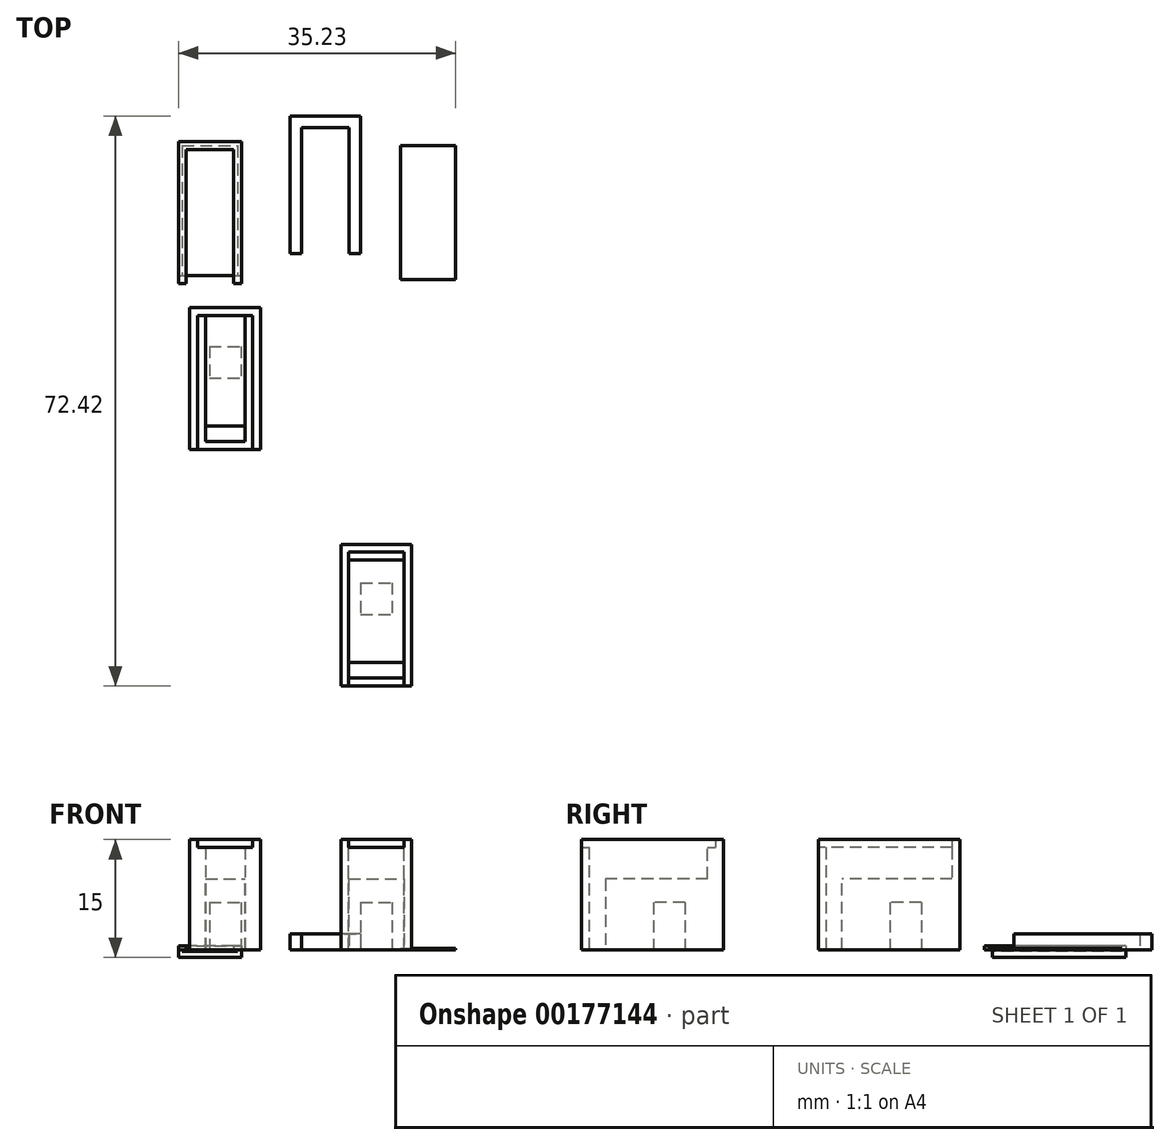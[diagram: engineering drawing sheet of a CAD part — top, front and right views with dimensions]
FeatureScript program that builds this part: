
annotation { "Feature Type Name" : "Feature", "Feature Type Description" : "" }
export const myFeature = defineFeature(function(context is Context, id is Id, definition is map)
    precondition{}
    {
        {
            var Q0;
            Q0=qCreatedBy(makeId("Top.planeOp"),FACE);
            var sketch = newSketch(context, id + "F0", { "sketchPlane" : qUnion([Q0])});
            skLineSegment(sketch, "E0.bottom", {"start": v(4.5, -9) * mm, "end": v(-4.5, -9) * mm});
            skLineSegment(sketch, "E0.top", {"start": v(4.5, 9) * mm, "end": v(-4.5, 9) * mm});
            skLineSegment(sketch, "E0.left", {"start": v(4.5, -9) * mm, "end": v(4.5, 9) * mm});
            skLineSegment(sketch, "E0.right", {"start": v(-4.5, -9) * mm, "end": v(-4.5, 9) * mm});
            skPoint(sketch, "E0.middle", {"position": v(0, 0) * mm});
            skSolve(sketch);
        }
        {
            var Q0;
            Q0 = qSketchRegion(id + "F0", true);
            extrude(context, id + "F1", {"entities" : qUnion([Q0]), "depth" : 13 * mm});
        }
        {
            var Q0;
            Q0=makeQuery(id+"F1.opExtrude","CAP_FACE",FACE,{"disambiguationData":[OSD([sQuery(id+"F0.wireOp",EDGE,"E0.bottom"),sQuery(id+"F0.wireOp",EDGE,"E0.top"),sQuery(id+"F0.wireOp",EDGE,"E0.left"),sQuery(id+"F0.wireOp",EDGE,"E0.right")])],"isStart":true});
            var sketch = newSketch(context, id + "F2", { "sketchPlane" : qUnion([Q0])});
            skLineSegment(sketch, "E1.bottom", {"start": v(-2, -4.1) * mm, "end": v(2, -4.1) * mm});
            skLineSegment(sketch, "E1.top", {"start": v(-2, -0.1) * mm, "end": v(2, -0.1) * mm});
            skLineSegment(sketch, "E1.left", {"start": v(-2, -4.1) * mm, "end": v(-2, -0.1) * mm});
            skLineSegment(sketch, "E1.right", {"start": v(2, -4.1) * mm, "end": v(2, -0.1) * mm});
            skPoint(sketch, "E1.middle", {"position": v(0, -2.1) * mm});
            skSolve(sketch);
        }
        {
            var Q0;
            Q0 = qSketchRegion(id + "F2", true);
            extrude(context, id + "F3", {"entities" : qUnion([Q0]), "operationType" : NewBodyOperationType.REMOVE, "oppositeDirection" : true, "depth" : 6 * mm});
        }
        {
            var Q0;
            Q0=makeQuery(id+"F1.opExtrude","SWEPT_FACE",FACE,{"disambiguationData":[OSD([sQuery(id+"F0.wireOp",EDGE,"E0.bottom")])]});
            var sketch = newSketch(context, id + "F4", { "sketchPlane" : qUnion([Q0])});
            skLineSegment(sketch, "E2.bottom", {"start": v(-2.5, 13) * mm, "end": v(2.5, 13) * mm});
            skLineSegment(sketch, "E2.top", {"start": v(-2.5, 9) * mm, "end": v(2.5, 9) * mm});
            skLineSegment(sketch, "E2.left", {"start": v(-2.5, 13) * mm, "end": v(-2.5, 9) * mm});
            skLineSegment(sketch, "E2.right", {"start": v(2.5, 13) * mm, "end": v(2.5, 9) * mm});
            skSolve(sketch);
        }
        {
            var Q0;
            Q0 = qSketchRegion(id + "F4", true);
            extrude(context, id + "F5", {"entities" : qUnion([Q0]), "operationType" : NewBodyOperationType.REMOVE, "oppositeDirection" : true, "depth" : 17 * mm});
        }
        {
            var Q0;
            Q0=qCreatedBy(makeId("Top.planeOp"),FACE);
            var sketch = newSketch(context, id + "F6", { "sketchPlane" : qUnion([Q0])});
            skLineSegment(sketch, "E3", {"start": v(-5.95, 12.1) * mm, "end": v(-5.95, 30.1) * mm});
            skLineSegment(sketch, "E4", {"start": v(-5.95, 30.1) * mm, "end": v(2.05, 30.1) * mm});
            skLineSegment(sketch, "E5", {"start": v(2.05, 30.1) * mm, "end": v(2.05, 12.1) * mm});
            skLineSegment(sketch, "E6", {"start": v(2.05, 12.1) * mm, "end": v(1.05, 12.1) * mm});
            skLineSegment(sketch, "E7", {"start": v(1.05, 12.1) * mm, "end": v(1.05, 29.1) * mm});
            skLineSegment(sketch, "E8", {"start": v(1.05, 29.1) * mm, "end": v(-4.95, 29.1) * mm});
            skLineSegment(sketch, "E9", {"start": v(-4.95, 29.1) * mm, "end": v(-4.95, 12.1) * mm});
            skLineSegment(sketch, "E10", {"start": v(-4.95, 12.1) * mm, "end": v(-5.95, 12.1) * mm});
            skSolve(sketch);
        }
        {
            var Q0;
            Q0 = qSketchRegion(id + "F6", true);
            extrude(context, id + "F7", {"entities" : qUnion([Q0]), "depth" : 0.5 * mm});
        }
        {
            var Q0;
            Q0=qCreatedBy(makeId("Top.planeOp"),FACE);
            var sketch = newSketch(context, id + "F8", { "sketchPlane" : qUnion([Q0])});
            skLineSegment(sketch, "E11.bottom", {"start": v(-5.95, 13.1) * mm, "end": v(2.05, 13.1) * mm});
            skLineSegment(sketch, "E11.top", {"start": v(-5.95, 30.1) * mm, "end": v(2.05, 30.1) * mm});
            skLineSegment(sketch, "E11.left", {"start": v(-5.95, 13.1) * mm, "end": v(-5.95, 30.1) * mm});
            skLineSegment(sketch, "E11.right", {"start": v(2.05, 13.1) * mm, "end": v(2.05, 30.1) * mm});
            skSolve(sketch);
        }
        {
            var Q0;
            Q0 = qSketchRegion(id + "F8", true);
            extrude(context, id + "F9", {"entities" : qUnion([Q0]), "oppositeDirection" : true, "depth" : 1 * mm});
        }
        {
            var Q0;
            Q0=makeQuery(id+"F9.opExtrude","SWEPT_FACE",FACE,{"disambiguationData":[OSD([sQuery(id+"F8.wireOp",EDGE,"E11.bottom")])]});
            var sketch = newSketch(context, id + "F10", { "sketchPlane" : qUnion([Q0])});
            skLineSegment(sketch, "E12.bottom", {"start": v(-5.45, 0) * mm, "end": v(1.55, 0) * mm});
            skLineSegment(sketch, "E12.top", {"start": v(-5.45, -0.2) * mm, "end": v(1.55, -0.2) * mm});
            skLineSegment(sketch, "E12.left", {"start": v(-5.45, 0) * mm, "end": v(-5.45, -0.2) * mm});
            skLineSegment(sketch, "E12.right", {"start": v(1.55, 0) * mm, "end": v(1.55, -0.2) * mm});
            skSolve(sketch);
        }
        {
            var Q0;
            Q0 = qSketchRegion(id + "F10", true);
            extrude(context, id + "F11", {"entities" : qUnion([Q0]), "operationType" : NewBodyOperationType.REMOVE, "oppositeDirection" : true, "depth" : 16.5 * mm});
        }
        {
            var Q0;
            Q0=qCreatedBy(makeId("Top.planeOp"),FACE);
            var sketch = newSketch(context, id + "F12", { "sketchPlane" : qUnion([Q0])});
            skLineSegment(sketch, "E13", {"start": v(8.22, 15.87) * mm, "end": v(8.22, 33.37) * mm});
            skLineSegment(sketch, "E14", {"start": v(8.22, 33.37) * mm, "end": v(17.22, 33.37) * mm});
            skLineSegment(sketch, "E15", {"start": v(17.22, 33.37) * mm, "end": v(17.22, 15.87) * mm});
            skLineSegment(sketch, "E16", {"start": v(17.22, 15.87) * mm, "end": v(15.72, 15.87) * mm});
            skLineSegment(sketch, "E17", {"start": v(15.72, 15.87) * mm, "end": v(15.72, 31.87) * mm});
            skLineSegment(sketch, "E18", {"start": v(15.72, 31.87) * mm, "end": v(9.72, 31.87) * mm});
            skLineSegment(sketch, "E19", {"start": v(9.72, 31.87) * mm, "end": v(9.72, 15.87) * mm});
            skLineSegment(sketch, "E20", {"start": v(9.72, 15.87) * mm, "end": v(8.22, 15.87) * mm});
            skSolve(sketch);
        }
        {
            var Q0;
            Q0 = qSketchRegion(id + "F12", true);
            extrude(context, id + "F13", {"entities" : qUnion([Q0]), "depth" : 2 * mm});
        }
        {
            var Q0;
            Q0=qCreatedBy(makeId("Top.planeOp"),FACE);
            var sketch = newSketch(context, id + "F14", { "sketchPlane" : qUnion([Q0])});
            skLineSegment(sketch, "E21.bottom", {"start": v(22.28, 12.58) * mm, "end": v(29.28, 12.58) * mm});
            skLineSegment(sketch, "E21.top", {"start": v(22.28, 29.58) * mm, "end": v(29.28, 29.58) * mm});
            skLineSegment(sketch, "E21.left", {"start": v(22.28, 12.58) * mm, "end": v(22.28, 29.58) * mm});
            skLineSegment(sketch, "E21.right", {"start": v(29.28, 12.58) * mm, "end": v(29.28, 29.58) * mm});
            skSolve(sketch);
        }
        {
            var Q0;
            Q0 = qSketchRegion(id + "F14", true);
            extrude(context, id + "F15", {"entities" : qUnion([Q0]), "depth" : 0.2 * mm});
        }
        {
            var Q0;
            Q0=makeQuery(id+"F5.boolean.opBoolean","COPY",FACE,{"derivedFrom":makeQuery(id+"F5.opExtrude","SWEPT_FACE",FACE,{"disambiguationData":[OSD([sQuery(id+"F4.wireOp",EDGE,"E2.top")])]})});
            var sketch = newSketch(context, id + "F16", { "sketchPlane" : qUnion([Q0])});
            skLineSegment(sketch, "E22.bottom", {"start": v(-2.5, -9) * mm, "end": v(2.5, -9) * mm});
            skLineSegment(sketch, "E22.top", {"start": v(-2.5, -6) * mm, "end": v(2.5, -6) * mm});
            skLineSegment(sketch, "E22.left", {"start": v(-2.5, -9) * mm, "end": v(-2.5, -6) * mm});
            skLineSegment(sketch, "E22.right", {"start": v(2.5, -9) * mm, "end": v(2.5, -6) * mm});
            skSolve(sketch);
        }
        {
            var Q0;
            Q0 = qSketchRegion(id + "F16", true);
            extrude(context, id + "F17", {"entities" : qUnion([Q0]), "operationType" : NewBodyOperationType.REMOVE, "oppositeDirection" : true, "depth" : 25 * mm});
        }
        {
            var Q0;
            Q0=makeQuery(id+"F1.opExtrude","CAP_FACE",FACE,{"disambiguationData":[OSD([sQuery(id+"F0.wireOp",EDGE,"E0.bottom"),sQuery(id+"F0.wireOp",EDGE,"E0.top"),sQuery(id+"F0.wireOp",EDGE,"E0.left"),sQuery(id+"F0.wireOp",EDGE,"E0.right")])],"isStart":false});
            var sketch = newSketch(context, id + "F18", { "sketchPlane" : qUnion([Q0])});
            skLineSegment(sketch, "E23", {"start": v(-4.5, -9) * mm, "end": v(-4.5, 9) * mm});
            skLineSegment(sketch, "E24", {"start": v(-4.5, 9) * mm, "end": v(4.5, 9) * mm});
            skLineSegment(sketch, "E25", {"start": v(4.5, 9) * mm, "end": v(4.5, -9) * mm});
            skLineSegment(sketch, "E26", {"start": v(4.5, -9) * mm, "end": v(3.5, -9) * mm});
            skLineSegment(sketch, "E27", {"start": v(3.5, -9) * mm, "end": v(3.5, 8) * mm});
            skLineSegment(sketch, "E28", {"start": v(3.5, 8) * mm, "end": v(-3.5, 8) * mm});
            skLineSegment(sketch, "E29", {"start": v(-3.5, 8) * mm, "end": v(-3.5, -9) * mm});
            skLineSegment(sketch, "E30", {"start": v(-3.5, -9) * mm, "end": v(-4.5, -9) * mm});
            skSolve(sketch);
        }
        {
            var Q0;
            Q0 = qSketchRegion(id + "F18", true);
            extrude(context, id + "F19", {"entities" : qUnion([Q0]), "operationType" : NewBodyOperationType.ADD, "depth" : 1 * mm});
        }
        {
            var Q0;
            Q0=makeQuery(id+"F1.opExtrude","CAP_FACE",FACE,{"disambiguationData":[OSD([sQuery(id+"F0.wireOp",EDGE,"E0.bottom"),sQuery(id+"F0.wireOp",EDGE,"E0.top"),sQuery(id+"F0.wireOp",EDGE,"E0.left"),sQuery(id+"F0.wireOp",EDGE,"E0.right")])],"isStart":true});
            var sketch = newSketch(context, id + "F20", { "sketchPlane" : qUnion([Q0])});
            skLineSegment(sketch, "E31.bottom", {"start": v(2.5, 9) * mm, "end": v(-2.5, 9) * mm});
            skLineSegment(sketch, "E31.top", {"start": v(2.5, 8) * mm, "end": v(-2.5, 8) * mm});
            skLineSegment(sketch, "E31.left", {"start": v(2.5, 9) * mm, "end": v(2.5, 8) * mm});
            skLineSegment(sketch, "E31.right", {"start": v(-2.5, 9) * mm, "end": v(-2.5, 8) * mm});
            skSolve(sketch);
        }
        {
            var Q0;
            Q0 = qSketchRegion(id + "F20", true);
            extrude(context, id + "F21", {"entities" : qUnion([Q0]), "operationType" : NewBodyOperationType.ADD, "oppositeDirection" : true, "depth" : 13 * mm});
        }
        {
            var Q0;
            Q0=qCreatedBy(makeId("Top.planeOp"),FACE);
            var sketch = newSketch(context, id + "F22", { "sketchPlane" : qUnion([Q0])});
            skLineSegment(sketch, "E32.bottom", {"start": v(23.68, -21.05) * mm, "end": v(14.68, -21.05) * mm});
            skLineSegment(sketch, "E32.top", {"start": v(23.68, -39.05) * mm, "end": v(14.68, -39.05) * mm});
            skLineSegment(sketch, "E32.left", {"start": v(23.68, -21.05) * mm, "end": v(23.68, -39.05) * mm});
            skLineSegment(sketch, "E32.right", {"start": v(14.68, -21.05) * mm, "end": v(14.68, -39.05) * mm});
            skPoint(sketch, "E32.middle", {"position": v(19.18, -30.05) * mm});
            skSolve(sketch);
        }
        {
            var Q0;
            Q0 = qSketchRegion(id + "F22", true);
            extrude(context, id + "F23", {"entities" : qUnion([Q0]), "depth" : 13 * mm});
        }
        {
            var Q0;
            Q0=makeQuery(id+"F23.opExtrude","CAP_FACE",FACE,{"disambiguationData":[OSD([sQuery(id+"F22.wireOp",EDGE,"E32.bottom"),sQuery(id+"F22.wireOp",EDGE,"E32.top"),sQuery(id+"F22.wireOp",EDGE,"E32.left"),sQuery(id+"F22.wireOp",EDGE,"E32.right")])],"isStart":false});
            var sketch = newSketch(context, id + "F24", { "sketchPlane" : qUnion([Q0])});
            skLineSegment(sketch, "E33.bottom", {"start": v(15.68, -23.05) * mm, "end": v(22.68, -23.05) * mm});
            skLineSegment(sketch, "E33.top", {"start": v(15.68, -38.05) * mm, "end": v(22.68, -38.05) * mm});
            skLineSegment(sketch, "E33.left", {"start": v(15.68, -23.05) * mm, "end": v(15.68, -38.05) * mm});
            skLineSegment(sketch, "E33.right", {"start": v(22.68, -23.05) * mm, "end": v(22.68, -38.05) * mm});
            skSolve(sketch);
        }
        {
            var Q0;
            Q0 = qSketchRegion(id + "F24", true);
            extrude(context, id + "F25", {"entities" : qUnion([Q0]), "operationType" : NewBodyOperationType.REMOVE, "oppositeDirection" : true, "depth" : 4 * mm});
        }
        {
            var Q0;
            Q0=makeQuery(id+"F23.opExtrude","CAP_FACE",FACE,{"disambiguationData":[OSD([sQuery(id+"F22.wireOp",EDGE,"E32.bottom"),sQuery(id+"F22.wireOp",EDGE,"E32.top"),sQuery(id+"F22.wireOp",EDGE,"E32.left"),sQuery(id+"F22.wireOp",EDGE,"E32.right")])],"isStart":true});
            var sketch = newSketch(context, id + "F26", { "sketchPlane" : qUnion([Q0])});
            skLineSegment(sketch, "E34.bottom", {"start": v(17.18, 25.95) * mm, "end": v(21.18, 25.95) * mm});
            skLineSegment(sketch, "E34.top", {"start": v(17.18, 29.95) * mm, "end": v(21.18, 29.95) * mm});
            skLineSegment(sketch, "E34.left", {"start": v(17.18, 25.95) * mm, "end": v(17.18, 29.95) * mm});
            skLineSegment(sketch, "E34.right", {"start": v(21.18, 25.95) * mm, "end": v(21.18, 29.95) * mm});
            skPoint(sketch, "E34.middle", {"position": v(19.18, 27.95) * mm});
            skLineSegment(sketch, "E35.bottom", {"start": v(22.68, 36.05) * mm, "end": v(15.68, 36.05) * mm});
            skLineSegment(sketch, "E35.top", {"start": v(22.68, 38.05) * mm, "end": v(15.68, 38.05) * mm});
            skLineSegment(sketch, "E35.left", {"start": v(22.68, 36.05) * mm, "end": v(22.68, 38.05) * mm});
            skLineSegment(sketch, "E35.right", {"start": v(15.68, 36.05) * mm, "end": v(15.68, 38.05) * mm});
            skPoint(sketch, "E35.middle", {"position": v(19.18, 37.05) * mm});
            skSolve(sketch);
        }
        {
            var Q0;
            Q0=makeQuery(id+"F26.imprint","IMPRINT",FACE,{"disambiguationData":[TD([[makeQuery(id+"F26.imprint","IMPRINT",EDGE,{"derivedFrom":sQuery(id+"F26.wireOp",EDGE,"E34.bottom")}),1.0]])]});
            extrude(context, id + "F27", {"entities" : qUnion([Q0]), "operationType" : NewBodyOperationType.REMOVE, "oppositeDirection" : true, "depth" : 6 * mm});
        }
        {
            var Q0;
            Q0=makeQuery(id+"F26.imprint","IMPRINT",FACE,{"disambiguationData":[TD([[makeQuery(id+"F26.imprint","IMPRINT",EDGE,{"derivedFrom":sQuery(id+"F26.wireOp",EDGE,"E35.bottom")}),-1.0]])]});
            extrude(context, id + "F28", {"entities" : qUnion([Q0]), "operationType" : NewBodyOperationType.REMOVE, "oppositeDirection" : true, "depth" : 9 * mm});
        }
        {
            var Q0;
            Q0=makeQuery(id+"F23.opExtrude","CAP_FACE",FACE,{"disambiguationData":[OSD([sQuery(id+"F22.wireOp",EDGE,"E32.bottom"),sQuery(id+"F22.wireOp",EDGE,"E32.top"),sQuery(id+"F22.wireOp",EDGE,"E32.left"),sQuery(id+"F22.wireOp",EDGE,"E32.right")])],"isStart":false});
            var sketch = newSketch(context, id + "F29", { "sketchPlane" : qUnion([Q0])});
            skLineSegment(sketch, "E36", {"start": v(14.68, -39.05) * mm, "end": v(14.68, -21.05) * mm});
            skLineSegment(sketch, "E37", {"start": v(14.68, -21.05) * mm, "end": v(23.68, -21.05) * mm});
            skLineSegment(sketch, "E38", {"start": v(23.68, -21.05) * mm, "end": v(23.68, -39.05) * mm});
            skLineSegment(sketch, "E39", {"start": v(23.68, -39.05) * mm, "end": v(22.68, -39.05) * mm});
            skLineSegment(sketch, "E40", {"start": v(22.68, -39.05) * mm, "end": v(22.68, -22.05) * mm});
            skLineSegment(sketch, "E41", {"start": v(22.68, -22.05) * mm, "end": v(15.68, -22.05) * mm});
            skLineSegment(sketch, "E42", {"start": v(15.68, -22.05) * mm, "end": v(15.68, -39.05) * mm});
            skLineSegment(sketch, "E43", {"start": v(15.68, -39.05) * mm, "end": v(14.68, -39.05) * mm});
            skSolve(sketch);
        }
        {
            var Q0;
            Q0 = qSketchRegion(id + "F29", true);
            extrude(context, id + "F30", {"entities" : qUnion([Q0]), "operationType" : NewBodyOperationType.ADD, "depth" : 1 * mm});
        }
    });
